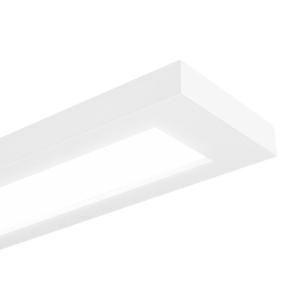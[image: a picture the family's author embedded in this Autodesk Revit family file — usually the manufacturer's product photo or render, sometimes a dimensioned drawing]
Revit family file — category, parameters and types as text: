
# Revit family: 3f_filippi_-_3f_travetta_op_3f_filippi_-_10735_-_3f_travetta_led_2x22w_op_l1590
name_source: partatom
category: Lighting Fixtures
units: mm (PartAtom-declared; Revit-internal decimal feet)

## family parameters
Cut with Voids When Loaded = No
Host = Face
Light Source = No
Part Type = Normal
Room Calculation Point = No
Round Connector Dimension = Use Diameter
Shared = No

## types (1)
- 3F Filippi - 3F Travetta OP (1 x LED, 5683 lm, 49 W, 4000 K)
    Apparent Load = 49 VA
    Approval mark = ENEC
    CIE Flux Codes = 49 81 97 100 100
    Color Rendering = 80
    Color Temperature = 4000 K
    Control Gear = Electronic ballast
    Default Elevation = 1800 mm
    Description = ILLUMINOTECHNICAL
Luminous efficiency 100% (DLOR 100%, ULOR 0%).
Initial luminous flux of the luminaire 5683 lm.
Direct symmetric distribution.
Installation Interdistance Transv.D = 1.19 x hu - Long.D = 1.20 x hu.
Tabular UGR (CIE 117 - 4H-8H; S=0.25H; 70/50/20): RUG 23.3 - 24.1.
Beam angle: 104° - 107°.
Luminous efficacy 116 lm/W.
Lifetime (L93/B10): 30000 h. (tq+25°C)
Lifetime (L90/B10): 50000 h. (tq+25°C)
Lifetime (L85/B10): 80000 h. (tq+25°C)
Lifetime (L80/B10): 100000 h. (tq+25°C)
Sudden decreased luminous flux after 50000 hours: 0% (C0).
Photobiological safety in compliance with IEC/TR 62778: RG0 risk exempt, (IEC 62471).
In compliance with IEC/EN 62722-2-1 - IEC/EN 62717 standards.

SOURCE
2 linear LED modules 22W/840.
Energy efficiency class (UE 2019/2020 - UE 2019/2015): D.
CIE 13.3 Colour rendering index: CRI >80 (R9 <50%).
IES TM-30 Fidelity Index: Rf = 84 Rg = 95.
CCT nominal colour temperature 4000 K.
Colour initial tolerance (MacAdam): SDCM 2.

MECHANICAL
Housing with squared shape in white painted galvannealed steel, with nonreflecting surface.
Flow recuperator in semi-glossy aluminium.
Opal methacrylate (PMMA) flat diffuser, anti-glare.
Luminaire with limited surface temperature. - D - (EN 60598-2-24)
Dimensions: 1590x190 mm, height 60 mm (edge 40 mm). Weight 5.21 kg.
IP20 protection degree.
Glow-wire test resistance 650°C.

ELECTRICAL
Halogen Free electronic wiring 230V-50/60Hz, power factor 0.95, THD <25%, constant output current, SELV, class I, 1 driver.
Power of the luminaire 49 W.
CE - IEC 60598-1 - EN 60598-1.
SAFE FLICKER: PstLM=<1 and SVM=<0.4 (IEC TR 61547-1 and IEC TR 63158), to ensure a more comfortable and safe light.
Luminaire compliant with EN 60598-2-22 for power supply from a centralised emergency system CPSS (Central Power Supply System), not incorporated in the luminaire - high risk areas excluded. The default power and flux are 100% in AC and 100% in DC.
Ambient temperature from 0°C to +25°C.
Temperature class T6 max 85°C.
5-pole terminal block for cascade line connection with connection capacity 2x2.5 mm².
Relative humidity UR: <85%.

INSTALLATION
Ceiling / Suspended.
All accessories dedicated to this product are available on the Catalog and on our website www.3F-Filippi.com.

APPLICATIONS
In environments, even with reduced height, requiring a comfortable light.
Exhibitions area, halls, great halls and shops.

WARNING
Luminaire designed for disposal/recycling at end-of-life.
Replaceable (LED only) light source by a professional. Replaceable control gear by a professional.
    Height = 60 mm
    Lamp = 1 x LED
    Lamp Light Flux = 5683 lm
    Lamp Power = 49 W
    Lamp count = 1
    Length = 1590 mm
    Lifetime = 50000 h
    Luminous efficacy = 116 lm/W
    Manufacturer = 3F Filippi
    ModVariant = No
    Model = 3F Filippi - 10735 - 3F Travetta LED 2x22W OP L1590
    Mounting Place = Ceiling
    Mounting Type = Pendant
    Number of Poles = 1
    OnlyDefault = Yes
    Power Factor = 1
    Product Name = 3F Filippi - 3F Travetta OP
    Product group = pendant luminaire
    ProductGroupID = 9
    Protection Class = Protection class I
    Protection Degree = IP 20
    RLX_Detail_Level = 1
    RLX_Emergency_Light_Flux = 0 lm
    RLX_Emergency_Type = 0
    RLX_Emergency_Type_DB = No
    RlxData = <blob elided: 32897 chars, md5=618d9947>
    Socket = socket
    Standby Power = 0 W
    System Light Flux = 5683 lm
    System Power = 49 W
    Type Comments = Product without accessories
    Type Image = 3ffilippi_3f_travetta_led_op.jpg
    URL = http://relux.com
    VarID = ---
    Voltage = 0 V
    Weight = 0.00 kg
    Width = 190 mm

## geometry (parser evidence)
native form markers: Blend x4, Sweep x10
no freeform markers — native parametric forms only
